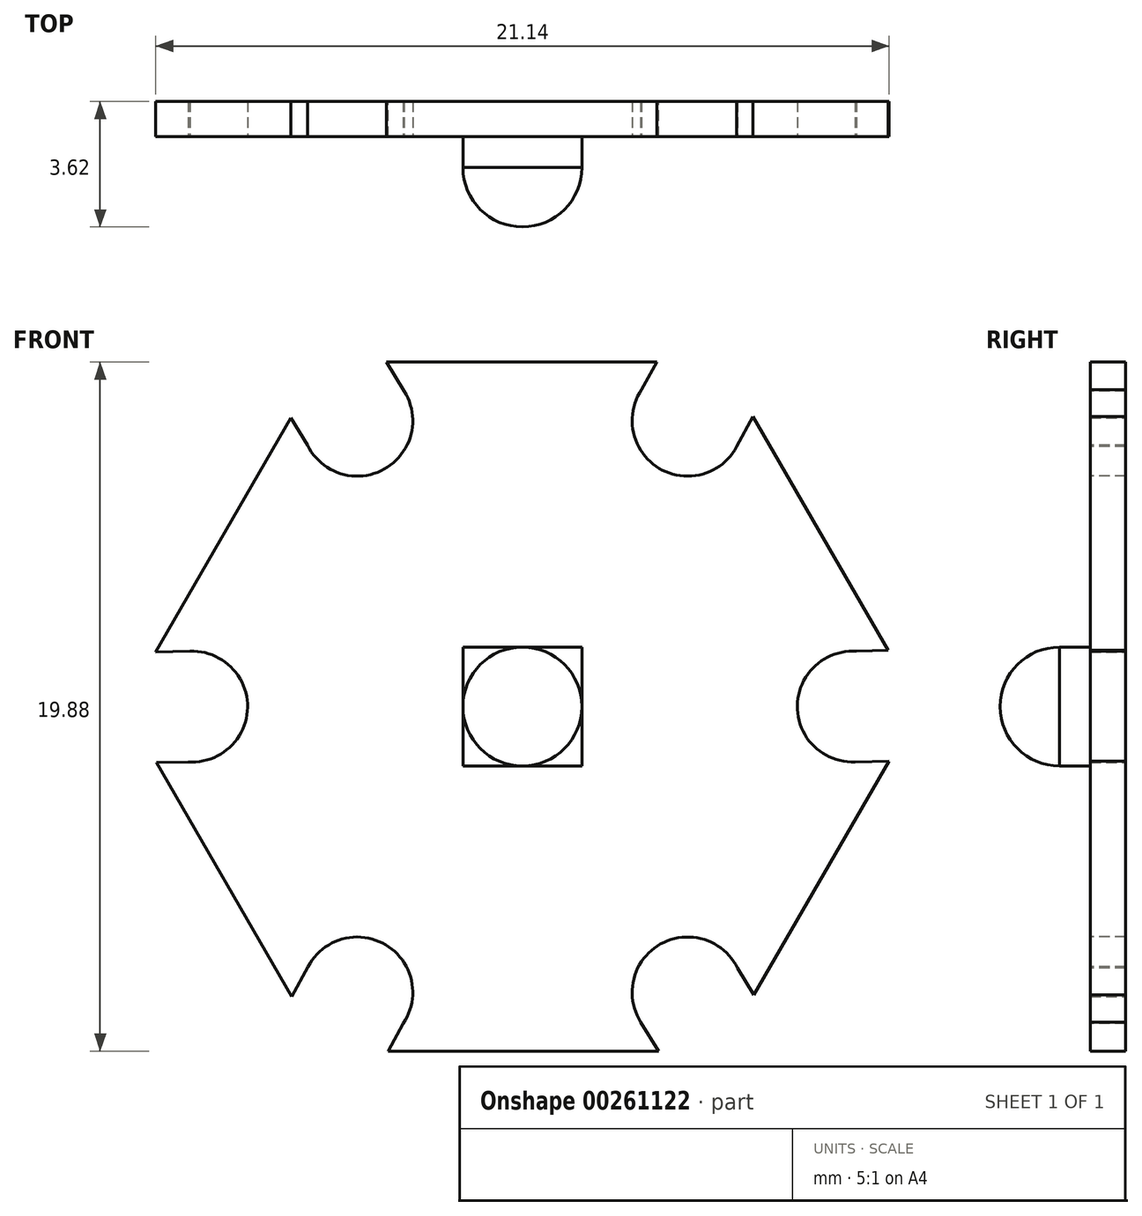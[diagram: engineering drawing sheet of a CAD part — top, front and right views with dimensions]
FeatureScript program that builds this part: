
annotation { "Feature Type Name" : "Feature", "Feature Type Description" : "" }
export const myFeature = defineFeature(function(context is Context, id is Id, definition is map)
    precondition{}
    {
        {
            var Q0;
            Q0=qCreatedBy(makeId("Front.planeOp"),FACE);
            var sketch = newSketch(context, id + "F0", { "sketchPlane" : qUnion([Q0])});
            skCircle(sketch, "E0.cCircle", {"center": v(0, 0) * mm, "radius": 9.94 * mm, "construction": true});
            skLineSegment(sketch, "E0.0", {"start": v(5.74, 9.94) * mm, "end": v(11.48, 0) * mm});
            skLineSegment(sketch, "E0.1", {"start": v(11.48, 0) * mm, "end": v(5.74, -9.94) * mm});
            skLineSegment(sketch, "E0.2", {"start": v(5.74, -9.94) * mm, "end": v(-5.74, -9.94) * mm});
            skLineSegment(sketch, "E0.3", {"start": v(-5.74, -9.94) * mm, "end": v(-11.48, 0) * mm});
            skLineSegment(sketch, "E0.4", {"start": v(-11.48, 0) * mm, "end": v(-5.74, 9.94) * mm});
            skLineSegment(sketch, "E0.5", {"start": v(-5.74, 9.94) * mm, "end": v(5.74, 9.94) * mm});
            skPoint(sketch, "E0.0.midPoint", {"position": v(8.61, 4.97) * mm});
            skSolve(sketch);
        }
        {
            var Q0;
            Q0 = qSketchRegion(id + "F0", true);
            extrude(context, id + "F1", {"entities" : qUnion([Q0]), "depth" : 1.02 * mm});
        }
        {
            var Q0;
            Q0=makeQuery(id+"F1.opExtrude","CAP_FACE",FACE,{"disambiguationData":[OSD([sQuery(id+"F0.wireOp",EDGE,"E0.0"),sQuery(id+"F0.wireOp",EDGE,"E0.1"),sQuery(id+"F0.wireOp",EDGE,"E0.2"),sQuery(id+"F0.wireOp",EDGE,"E0.3"),sQuery(id+"F0.wireOp",EDGE,"E0.4"),sQuery(id+"F0.wireOp",EDGE,"E0.5")])],"isStart":false});
            var sketch = newSketch(context, id + "F2", { "sketchPlane" : qUnion([Q0])});
            skCircle(sketch, "E1", {"center": v(-4.76, 8.25) * mm, "radius": 1.6 * mm});
            skLineSegment(sketch, "E2", {"start": v(0, 0) * mm, "end": v(-5.74, 9.94) * mm, "construction": true});
            skLineSegment(sketch, "E3", {"start": v(-3.4, 9.1) * mm, "end": v(-6.6, 14.31) * mm});
            skLineSegment(sketch, "E4", {"start": v(-6.2, 7.54) * mm, "end": v(-9.75, 13.35) * mm});
            skLineSegment(sketch, "E5", {"start": v(-9.75, 13.35) * mm, "end": v(-6.6, 14.31) * mm});
            skCircle(sketch, "E6.1.0", {"center": v(-9.53, 0) * mm, "radius": 1.6 * mm});
            skLineSegment(sketch, "E6.1.1", {"start": v(-9.59, 1.6) * mm, "end": v(-15.69, 1.44) * mm});
            skLineSegment(sketch, "E6.1.2", {"start": v(-16.44, -1.77) * mm, "end": v(-15.69, 1.44) * mm});
            skLineSegment(sketch, "E6.1.3", {"start": v(-9.63, -1.6) * mm, "end": v(-16.44, -1.77) * mm});
            skCircle(sketch, "E6.2.0", {"center": v(-4.76, -8.25) * mm, "radius": 1.6 * mm});
            skLineSegment(sketch, "E6.2.1", {"start": v(-6.18, -7.5) * mm, "end": v(-9.1, -12.87) * mm});
            skLineSegment(sketch, "E6.2.2", {"start": v(-6.69, -15.12) * mm, "end": v(-9.1, -12.87) * mm});
            skLineSegment(sketch, "E6.2.3", {"start": v(-3.43, -9.14) * mm, "end": v(-6.69, -15.12) * mm});
            skCircle(sketch, "E6.3.0", {"center": v(4.76, -8.25) * mm, "radius": 1.6 * mm});
            skLineSegment(sketch, "E6.3.1", {"start": v(3.4, -9.1) * mm, "end": v(6.6, -14.31) * mm});
            skLineSegment(sketch, "E6.3.2", {"start": v(9.75, -13.35) * mm, "end": v(6.6, -14.31) * mm});
            skLineSegment(sketch, "E6.3.3", {"start": v(6.2, -7.54) * mm, "end": v(9.75, -13.35) * mm});
            skCircle(sketch, "E6.4.0", {"center": v(9.53, 0) * mm, "radius": 1.6 * mm});
            skLineSegment(sketch, "E6.4.1", {"start": v(9.59, -1.6) * mm, "end": v(15.69, -1.44) * mm});
            skLineSegment(sketch, "E6.4.2", {"start": v(16.44, 1.77) * mm, "end": v(15.69, -1.44) * mm});
            skLineSegment(sketch, "E6.4.3", {"start": v(9.63, 1.6) * mm, "end": v(16.44, 1.77) * mm});
            skCircle(sketch, "E6.5.0", {"center": v(4.76, 8.25) * mm, "radius": 1.6 * mm});
            skLineSegment(sketch, "E6.5.1", {"start": v(6.18, 7.5) * mm, "end": v(9.1, 12.87) * mm});
            skLineSegment(sketch, "E6.5.2", {"start": v(6.69, 15.12) * mm, "end": v(9.1, 12.87) * mm});
            skLineSegment(sketch, "E6.5.3", {"start": v(3.43, 9.14) * mm, "end": v(6.69, 15.12) * mm});
            skPoint(sketch, "E6.center", {"position": v(0, 0) * mm});
            skPoint(sketch, "E7", {"position": v(-3.92, 9.94) * mm});
            skPoint(sketch, "E8", {"position": v(3.87, 9.94) * mm});
            skSolve(sketch);
        }
        {
            var Q0;
            Q0 = qSketchRegion(id + "F2", true);
            extrude(context, id + "F3", {"entities" : qUnion([Q0]), "operationType" : NewBodyOperationType.REMOVE, "oppositeDirection" : true, "depth" : 25.4 * mm});
        }
        {
            var Q0;
            Q0=makeQuery(id+"F1.opExtrude","CAP_FACE",FACE,{"disambiguationData":[OSD([sQuery(id+"F0.wireOp",EDGE,"E0.0"),sQuery(id+"F0.wireOp",EDGE,"E0.1"),sQuery(id+"F0.wireOp",EDGE,"E0.2"),sQuery(id+"F0.wireOp",EDGE,"E0.3"),sQuery(id+"F0.wireOp",EDGE,"E0.4"),sQuery(id+"F0.wireOp",EDGE,"E0.5")])],"isStart":false});
            var sketch = newSketch(context, id + "F4", { "sketchPlane" : qUnion([Q0])});
            skLineSegment(sketch, "E9.bottom", {"start": v(1.71, 1.71) * mm, "end": v(-1.71, 1.71) * mm});
            skLineSegment(sketch, "E9.top", {"start": v(1.71, -1.71) * mm, "end": v(-1.71, -1.71) * mm});
            skLineSegment(sketch, "E9.left", {"start": v(1.71, 1.71) * mm, "end": v(1.71, -1.71) * mm});
            skLineSegment(sketch, "E9.right", {"start": v(-1.71, 1.71) * mm, "end": v(-1.71, -1.71) * mm});
            skPoint(sketch, "E9.middle", {"position": v(0, 0) * mm});
            skSolve(sketch);
        }
        {
            var Q0;
            Q0=makeQuery(id+"F4.imprint","IMPRINT",FACE,{"disambiguationData":[TD([[makeQuery(id+"F4.imprint","IMPRINT",EDGE,{"derivedFrom":sQuery(id+"F4.wireOp",EDGE,"E9.bottom")}),1.0]])]});
            extrude(context, id + "F5", {"entities" : qUnion([Q0]), "operationType" : NewBodyOperationType.ADD, "depth" : 0.89 * mm});
        }
        {
            var Q0;
            Q0=makeQuery(id+"F5.opExtrude","CAP_FACE",FACE,{"disambiguationData":[OSD([sQuery(id+"F4.wireOp",EDGE,"E9.bottom"),sQuery(id+"F4.wireOp",EDGE,"E9.top"),sQuery(id+"F4.wireOp",EDGE,"E9.left"),sQuery(id+"F4.wireOp",EDGE,"E9.right")])],"isStart":false});
            var sketch = newSketch(context, id + "F6", { "sketchPlane" : qUnion([Q0])});
            skArc(sketch, "E10", {"start": v(1.71, 0) * mm, "mid": v(0, 1.71) * mm, "end": v(-1.71, 0) * mm});
            skLineSegment(sketch, "E11", {"start": v(-1.71, 0) * mm, "end": v(1.71, 0) * mm});
            skSolve(sketch);
        }
        {
            var Q0;
            {var subQ0=sQuery(id+"F6.wireOp",EDGE,"E11");Q0=makeQuery(id+"F6.imprint","IMPRINT",FACE,{"disambiguationData":[TD([[makeQuery(id+"F6.imprint","IMPRINT",EDGE,{"derivedFrom":subQ0}),1.0]])]});}
            var Q1;
            Q1=sQuery(id+"F6.wireOp",EDGE,"E11");
            revolve(context, id + "F7", {"operationType" : NewBodyOperationType.ADD, "entities" : qUnion([Q0]), "axis" : qUnion([Q1]), "revolveType" : RevolveType.FULL});
        }
    });
